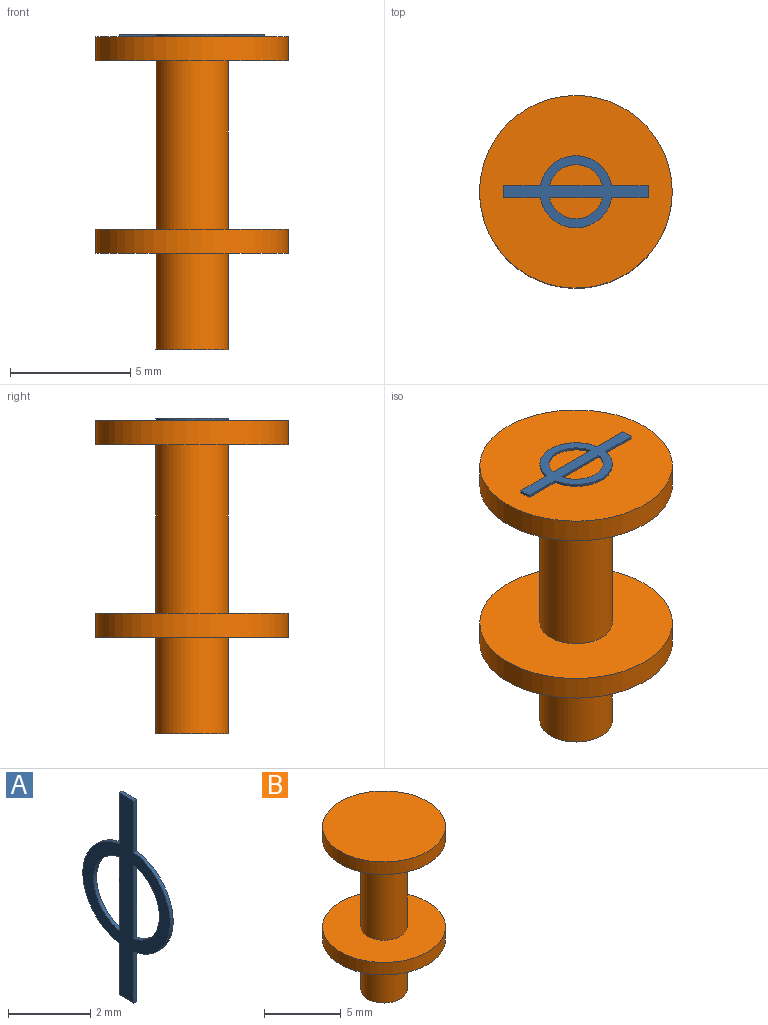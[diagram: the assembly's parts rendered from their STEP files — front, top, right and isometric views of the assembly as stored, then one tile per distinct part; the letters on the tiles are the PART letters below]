
ASSEMBLY  parts=2 mates=1
PART A: 14 faces, bbox 0.1x3x6 mm
  f0: plane 2.19x0.1mm, normal (0,-1,0), area 0.2mm2, adj f11,f12,f13
  f1: plane 2.19x0.1mm, normal (0,1,0), area 0.2mm2, adj f9,f12,f13
  f2: cylinder r=1.5mm len=2.96mm, axis (1,0,0), area 0.4mm2, adj f3,f10,f12,f13
  f3: plane 1.52x0.1mm, normal (0,1,0), area 0.2mm2, adj f2,f4,f12,f13
  f4: plane 0.5x0.1mm, normal (0,0,-1), area 0.1mm2, adj f3,f5,f12,f13
  f5: plane 1.52x0.1mm, normal (0,-1,0), area 0.2mm2, adj f4,f6,f12,f13
  f6: cylinder r=1.5mm len=2.96mm, axis (1,0,0), area 0.4mm2, adj f5,f7,f12,f13
  f7: plane 1.52x0.1mm, normal (0,-1,0), area 0.2mm2, adj f6,f8,f12,f13
  f8: plane 0.5x0.1mm, normal (0,0,1), area 0.1mm2, adj f7,f10,f12,f13
  f9: cylinder r=1.12mm len=2.19mm, axis (1,0,0), area 0.3mm2, adj f1,f12,f13
  f10: plane 1.52x0.1mm, normal (0,1,0), area 0.2mm2, adj f2,f8,f12,f13
  f11: cylinder r=1.12mm len=2.19mm, axis (1,0,0), area 0.3mm2, adj f0,f12,f13
  f12: plane 6x3mm, normal (-1,0,0), area 5.7mm2, adj f0,f1,f2,f3,f4,f5,f6,f7
  f13: plane 6x3mm, normal (1,0,0), area 5.7mm2, adj f0,f1,f2,f3,f4,f5,f6,f7
PART B: 9 faces, bbox 8x8x13 mm
  f0: plane 3x3mm, normal (0,0,-1), area 7.1mm2, adj f1
  f1: cylinder r=1.5mm len=4mm, axis (0,0,1), area 37.7mm2, adj f0,f2
  f2: plane 8x8mm, normal (0,0,-1), area 43.2mm2, adj f1,f3
  f3: cylinder r=4mm len=8mm, axis (0,0,1), area 25.1mm2, adj f2,f4
  f4: plane 8x8mm, normal (0,0,1), area 43.2mm2, adj f3,f5
  f5: cylinder r=1.5mm len=7mm, axis (0,0,1), area 66mm2, adj f4,f6
  f6: plane 8x8mm, normal (0,0,-1), area 43.2mm2, adj f5,f7
  f7: cylinder r=4mm len=8mm, axis (0,0,1), area 25.1mm2, adj f6,f8
  f8: plane 8x8mm, normal (0,0,1), area 50.3mm2, adj f7
PLACE A rot(axis=(0,1,0),90deg) t=(-7.11,2.14,-61.58)mm
PLACE B t=(7.03,2.14,-2.88)mm
MATE fastened B.f1 <-> A.f2  axis (0,0,1) through (7.03,2.14,10.12)mm
